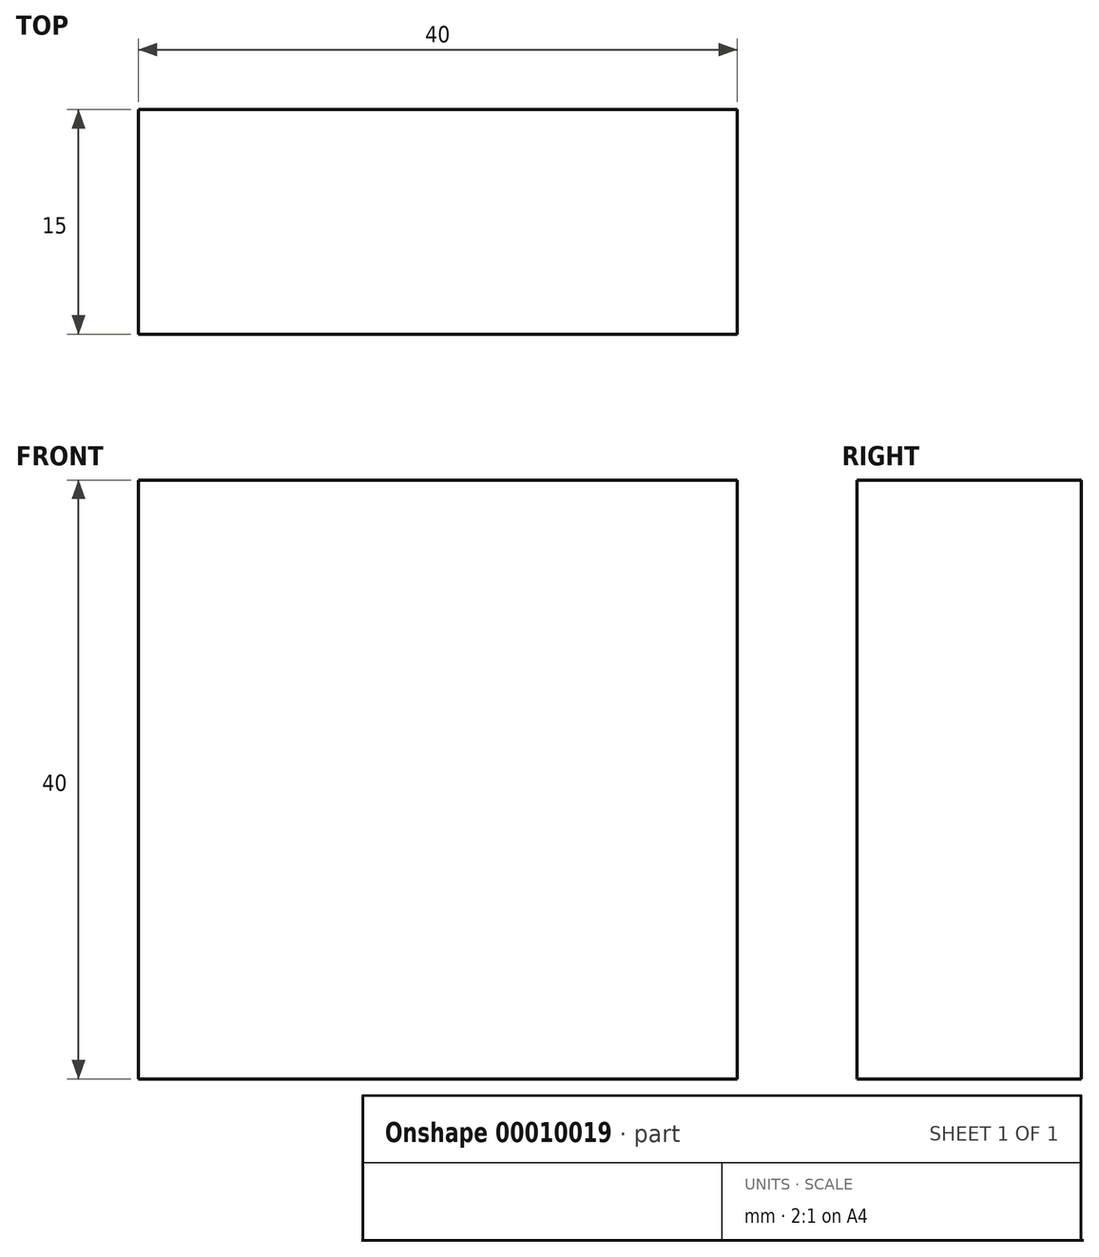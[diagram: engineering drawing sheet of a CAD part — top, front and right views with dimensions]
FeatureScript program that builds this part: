
annotation { "Feature Type Name" : "Feature", "Feature Type Description" : "" }
export const myFeature = defineFeature(function(context is Context, id is Id, definition is map)
    precondition{}
    {
        {
            var Q0;
            Q0=qCreatedBy(makeId("Front.planeOp"),FACE);
            var sketch = newSketch(context, id + "F0", { "sketchPlane" : qUnion([Q0])});
            skLineSegment(sketch, "E0.bottom", {"start": v(0, 40) * mm, "end": v(40, 40) * mm});
            skLineSegment(sketch, "E0.top", {"start": v(0, 0) * mm, "end": v(40, 0) * mm});
            skLineSegment(sketch, "E0.left", {"start": v(0, 40) * mm, "end": v(0, 0) * mm});
            skLineSegment(sketch, "E0.right", {"start": v(40, 40) * mm, "end": v(40, 0) * mm});
            skSolve(sketch);
        }
        {
            var Q0;
            Q0=makeQuery(id+"F0.imprint","IMPRINT",FACE,{"disambiguationData":[TD([[makeQuery(id+"F0.imprint","IMPRINT",EDGE,{"derivedFrom":sQuery(id+"F0.wireOp",EDGE,"E0.bottom")}),-1.0]])]});
            extrude(context, id + "F1", {"entities" : qUnion([Q0]), "depth" : 15 * mm});
        }
    });
